# Revit family: Paper_Holder-GROHE-Starlight-41068_Series
name_source: partatom
category: Plumbing Fixtures
revit_build: Autodesk Revit 2016 (Build: 20150714_1515(x64)
units: mm (PartAtom-declared; Revit-internal decimal feet)

## family parameters
Cut with Voids When Loaded = No
Host = Face
OmniClass Number = 23.40.20.21.27
OmniClass Title = Towel Bars
Part Type = Normal
Room Calculation Point = No
Round Connector Dimension = Use Diameter
Shared = Yes

## types (5) — shared parameters
Assembly Code = D2010710
CW Connection = No
Default Elevation = 0"
Description = Paper Holder w/ Cover
HW Connection = No
Height = 9/16"
Installation Type = Wall Mounted
Length = 6"
Manufacturer = Grohe
Price = Prices may vary. Please consult Manufacturer Representative for most up-to-date price list.
URL = https://www.grohe.us
Vent Connection = No
Warranty Documentation Link = https://cdn.cloud.grohe.com
Waste Connection = No
Width = 3 3/8"
zero-valued in all types: CWFU, HWFU, WFU

## per-type parameters (varying)
| type | Finish | Material | Model |
| 41068000 | Metal-Grohe-000-Starlight Chrome | Metal-Grohe-000-Starlight Chrome | 41068000 |
| 41068A00 | Metal-Grohe-A00-Hard Graphite | Metal-Grohe-A00-Hard Graphite | 41068A00 |
| 41068BE0 | Metal-Grohe-BE0-Polished Nickel | Metal-Grohe-BE0-Polished Nickel | 41068BE0 |
| 41068EN0 | Metal-Grohe-EN0-Brushed Nickel | Metal-Grohe-EN0-Brushed Nickel | 41068EN0 |
| 41068GN0 | Metal-Grohe-GN0-Brushed Cool Sunrise | Metal-Grohe-GN0-Brushed Cool Sunrise | 41068GNO |

## geometry (parser evidence)
native form markers: Sweep x5
no freeform markers — native parametric forms only
